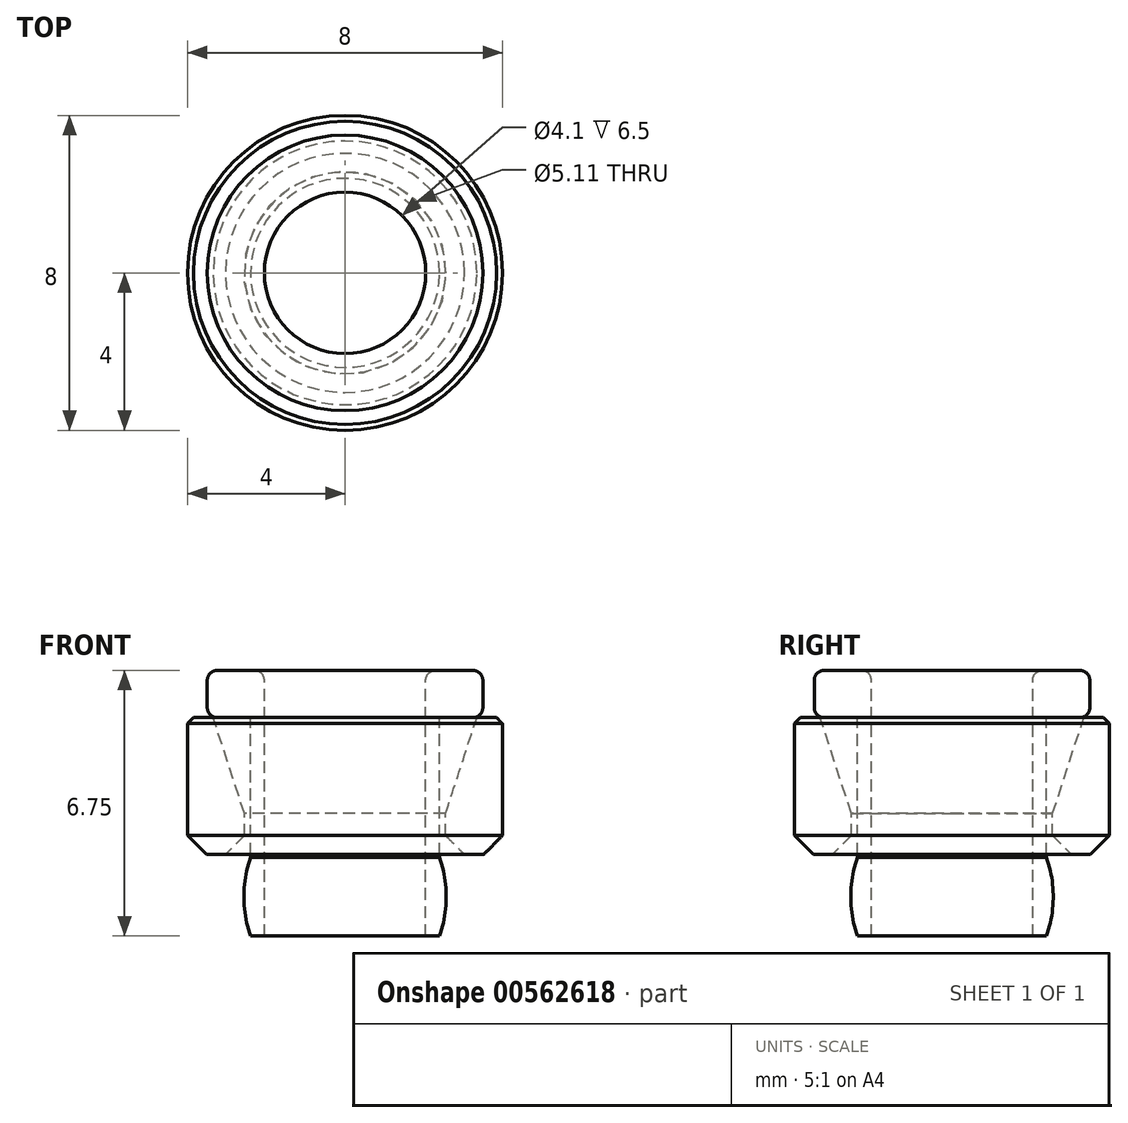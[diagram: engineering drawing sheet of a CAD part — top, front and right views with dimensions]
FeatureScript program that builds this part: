
annotation { "Feature Type Name" : "Feature", "Feature Type Description" : "" }
export const myFeature = defineFeature(function(context is Context, id is Id, definition is map)
    precondition{}
    {
        {
            var Q0;
            Q0=qCreatedBy(makeId("Front.planeOp"),FACE);
            var sketch = newSketch(context, id + "F0", { "sketchPlane" : qUnion([Q0])});
            skLineSegment(sketch, "E0", {"start": v(-3.35, 0) * mm, "end": v(-4, 0) * mm});
            skLineSegment(sketch, "E1", {"start": v(-4, 0) * mm, "end": v(-4, -3) * mm});
            skLineSegment(sketch, "E2", {"start": v(-3.52, -3.48) * mm, "end": v(-3.04, -3.48) * mm});
            skLineSegment(sketch, "E3", {"start": v(-2.56, -3) * mm, "end": v(-3.04, -3.48) * mm});
            skLineSegment(sketch, "E4", {"start": v(-2.56, -3) * mm, "end": v(-2.56, -2.43) * mm});
            skLineSegment(sketch, "E5", {"start": v(-3.35, 0) * mm, "end": v(-2.55, -2.43) * mm});
            skLineSegment(sketch, "E6", {"start": v(-4, -3) * mm, "end": v(-3.52, -3.48) * mm});
            skPoint(sketch, "E7.orphan", {"position": v(-4, -3.48) * mm});
            skLineSegment(sketch, "E8", {"start": v(-3.35, 0) * mm, "end": v(-3.35, -3.19) * mm, "construction": true});
            skLineSegment(sketch, "E9", {"start": v(0, 0) * mm, "end": v(0, -4.92) * mm, "construction": true});
            skSolve(sketch);
        }
        {
            var Q0;
            Q0=makeQuery(id+"F0.imprint","IMPRINT",FACE,{"disambiguationData":[TD([[makeQuery(id+"F0.imprint","IMPRINT",EDGE,{"derivedFrom":sQuery(id+"F0.wireOp",EDGE,"E0")}),1.0]])]});
            var Q1;
            Q1=sQuery(id+"F0.wireOp",EDGE,"E9");
            revolve(context, id + "F1", {"entities" : qUnion([Q0]), "axis" : qUnion([Q1]), "revolveType" : RevolveType.FULL});
        }
        {
            var Q0;
            Q0=makeQuery(id+"F1.opRevolve","SWEPT_EDGE",EDGE,{"disambiguationData":[OSD([sQuery(id+"F0.wireOp",EDGE,"E0"),sQuery(id+"F0.wireOp",EDGE,"E1")])]});
            chamfer(context, id + "F2", {"entities" : qUnion([Q0]), "width" : .15 * mm, "tangentPropagation" : true});
        }
        {
            var Q0;
            Q0=qCreatedBy(makeId("Front.planeOp"),FACE);
            var sketch = newSketch(context, id + "F3", { "sketchPlane" : qUnion([Q0])});
            skLineSegment(sketch, "E10", {"start": v(-2.4, 0) * mm, "end": v(-3.5, 0) * mm});
            skLineSegment(sketch, "E11", {"start": v(-3.5, 0) * mm, "end": v(-3.5, 1.2) * mm});
            skLineSegment(sketch, "E12", {"start": v(-3.5, 1.2) * mm, "end": v(-2.05, 1.2) * mm});
            skLineSegment(sketch, "E13", {"start": v(-2.05, 1.2) * mm, "end": v(-2.05, -5.55) * mm});
            skLineSegment(sketch, "E14", {"start": v(-2.05, -5.55) * mm, "end": v(-2.4, -5.55) * mm});
            skLineSegment(sketch, "E15", {"start": v(-2.4, -3.55) * mm, "end": v(-2.4, 0) * mm});
            skArc(sketch, "E16", {"start": v(-2.4, -3.55) * mm, "mid": v(-2.57, -4.55) * mm, "end": v(-2.4, -5.55) * mm});
            skLineSegment(sketch, "E17", {"start": v(0, 0) * mm, "end": v(0, -6.1) * mm, "construction": true});
            skSolve(sketch);
        }
        {
            var Q0;
            Q0=makeQuery(id+"F3.imprint","IMPRINT",FACE,{"disambiguationData":[TD([[makeQuery(id+"F3.imprint","IMPRINT",EDGE,{"derivedFrom":sQuery(id+"F3.wireOp",EDGE,"E10")}),-1.0]])]});
            var Q1;
            Q1=sQuery(id+"F3.wireOp",EDGE,"E17");
            revolve(context, id + "F4", {"entities" : qUnion([Q0]), "axis" : qUnion([Q1]), "revolveType" : RevolveType.FULL});
        }
        {
            var Q0;
            Q0=makeQuery(id+"F4.opRevolve","SWEPT_EDGE",EDGE,{"disambiguationData":[OSD([sQuery(id+"F3.wireOp",EDGE,"E11"),sQuery(id+"F3.wireOp",EDGE,"E12")])]});
            var Q1;
            Q1=makeQuery(id+"F4.opRevolve","SWEPT_EDGE",EDGE,{"disambiguationData":[OSD([sQuery(id+"F3.wireOp",EDGE,"E10"),sQuery(id+"F3.wireOp",EDGE,"E11")])]});
            var Q2;
            Q2=makeQuery(id+"F4.opRevolve","SWEPT_EDGE",EDGE,{"disambiguationData":[OSD([sQuery(id+"F3.wireOp",EDGE,"E12"),sQuery(id+"F3.wireOp",EDGE,"E13")])]});
            fillet(context, id + "F5", {"entities" : qUnion([Q0, Q1, Q2]), "radius" : .25 * mm, "tangentPropagation" : true, "allowEdgeOverflow" : false});
        }
    });
